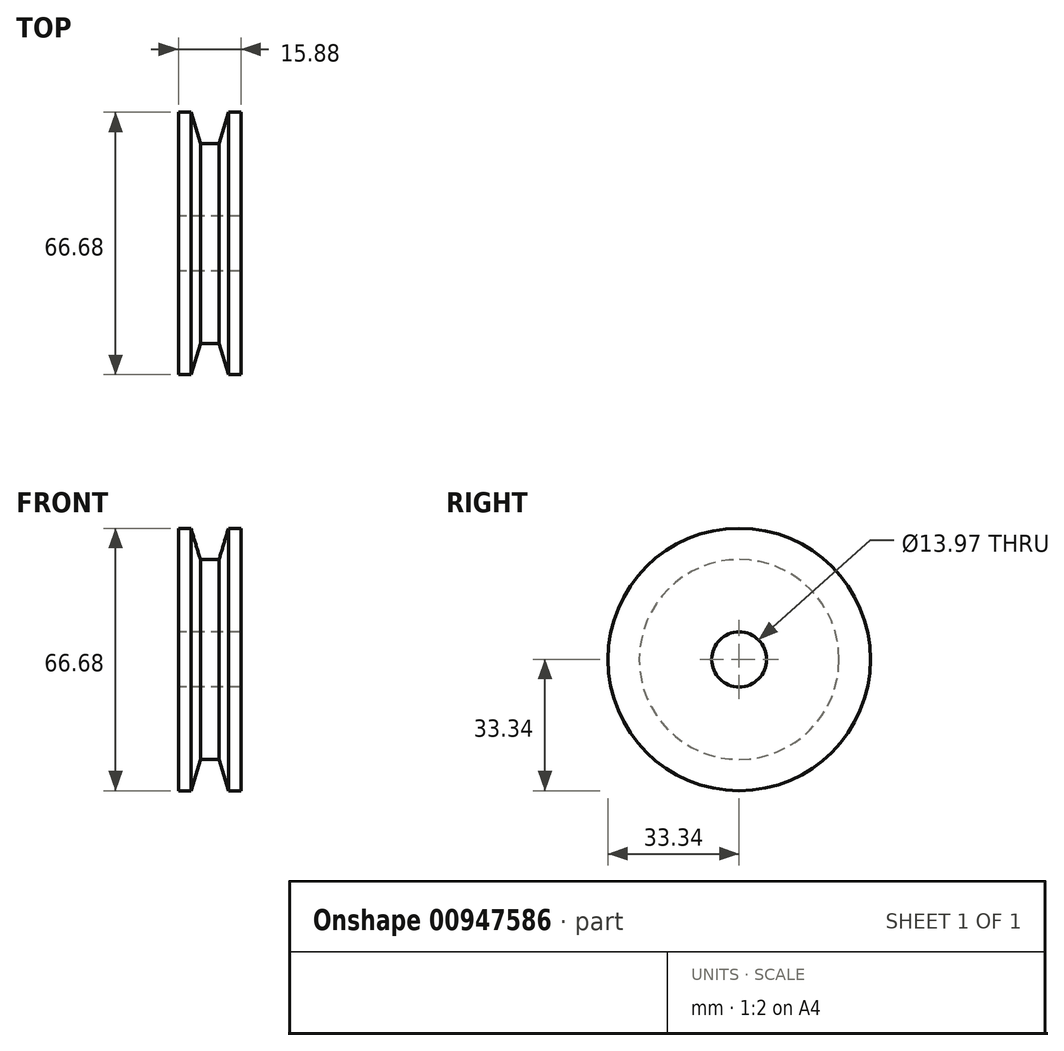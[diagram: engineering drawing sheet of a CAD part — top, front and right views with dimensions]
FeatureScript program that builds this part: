
annotation { "Feature Type Name" : "Feature", "Feature Type Description" : "" }
export const myFeature = defineFeature(function(context is Context, id is Id, definition is map)
    precondition{}
    {
        {
            var Q0;
            Q0=qCreatedBy(makeId("Front.planeOp"),FACE);
            var sketch = newSketch(context, id + "F0", { "sketchPlane" : qUnion([Q0])});
            skLineSegment(sketch, "E0.bottom", {"start": v(-7.94, 6.99) * mm, "end": v(7.94, 6.99) * mm});
            skLineSegment(sketch, "E0.top", {"start": v(-7.94, 33.34) * mm, "end": v(-4.76, 33.34) * mm});
            skLineSegment(sketch, "E0.left", {"start": v(-7.94, 6.99) * mm, "end": v(-7.94, 33.34) * mm});
            skLineSegment(sketch, "E0.right", {"start": v(7.94, 6.99) * mm, "end": v(7.94, 33.34) * mm});
            skLineSegment(sketch, "E1.trimOffspring", {"start": v(4.76, 33.34) * mm, "end": v(7.94, 33.34) * mm});
            skLineSegment(sketch, "E2", {"start": v(4.76, 33.34) * mm, "end": v(2.38, 25.4) * mm});
            skLineSegment(sketch, "E3", {"start": v(2.38, 25.4) * mm, "end": v(-2.38, 25.4) * mm});
            skLineSegment(sketch, "E4", {"start": v(-2.38, 25.4) * mm, "end": v(-4.76, 33.34) * mm});
            skSolve(sketch);
        }
        {
            var Q0;
            Q0=qCreatedBy(makeId("Front.planeOp"),FACE);
            var sketch = newSketch(context, id + "F1", { "sketchPlane" : qUnion([Q0])});
            skLineSegment(sketch, "E5", {"start": v(0, 0) * mm, "end": v(30.01, 0) * mm});
            skSolve(sketch);
        }
        {
            var Q0;
            Q0 = qSketchRegion(id + "F0", true);
            var Q1;
            Q1=sQuery(id+"F1.wireOp",EDGE,"E5");
            revolve(context, id + "F2", {"surfaceOperationType" : NewSurfaceOperationType.NEW, "entities" : qUnion([Q0]), "axis" : qUnion([Q1]), "revolveType" : RevolveType.FULL});
        }
    });
